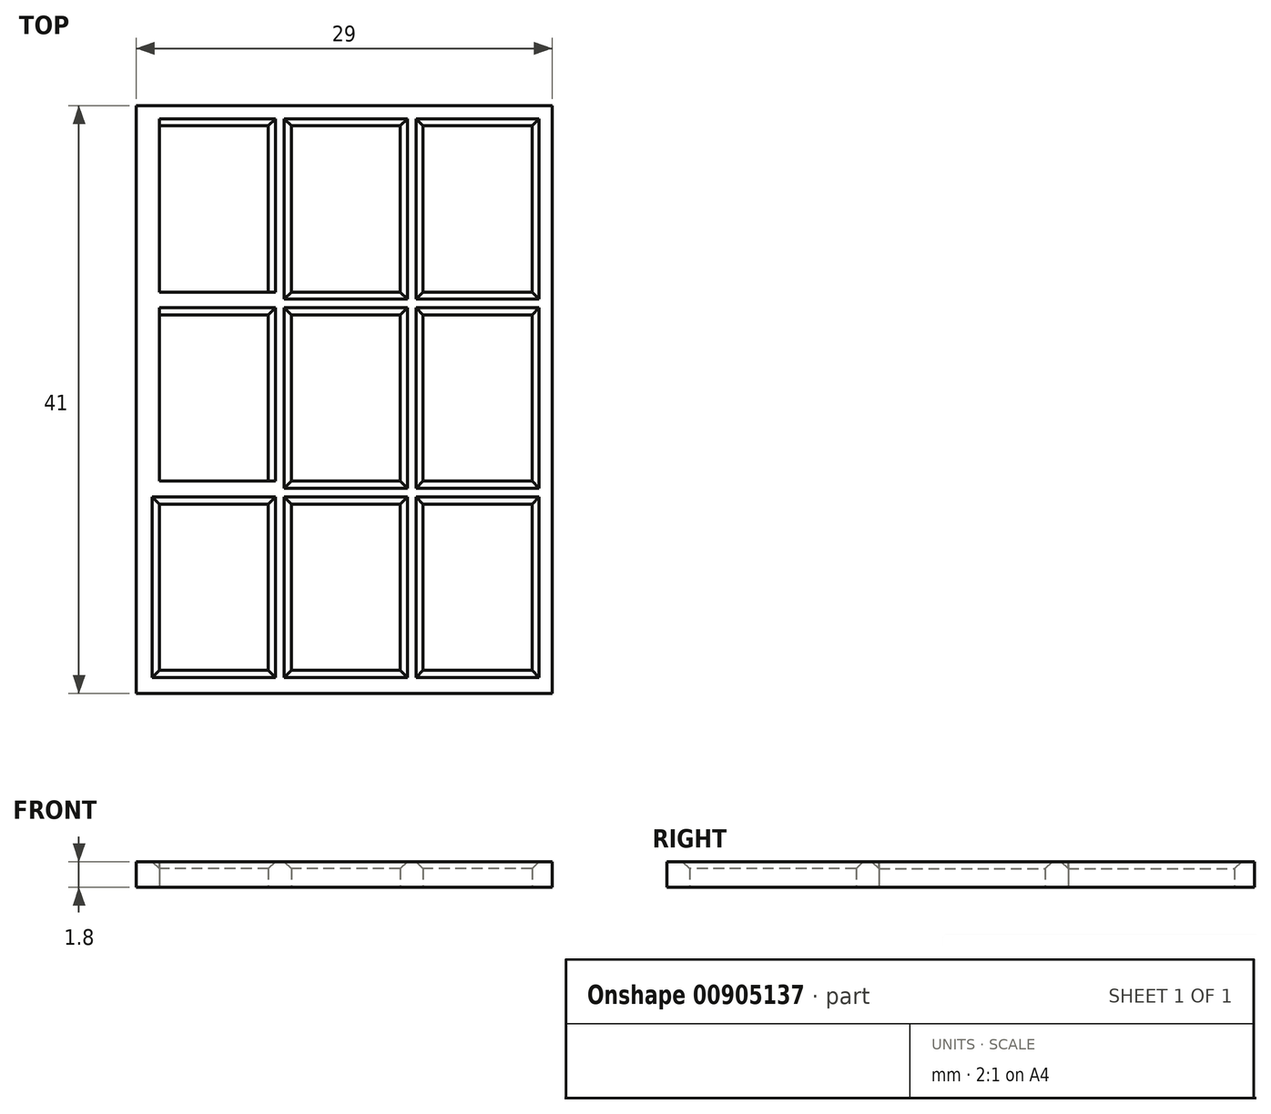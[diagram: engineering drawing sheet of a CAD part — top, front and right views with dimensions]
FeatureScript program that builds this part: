
annotation { "Feature Type Name" : "Feature", "Feature Type Description" : "" }
export const myFeature = defineFeature(function(context is Context, id is Id, definition is map)
    precondition{}
    {
        {
            var Q0;
            Q0=qCreatedBy(makeId("Top.planeOp"),FACE);
            var sketch = newSketch(context, id + "F0", { "sketchPlane" : qUnion([Q0])});
            skLineSegment(sketch, "E0.bottom", {"start": v(-14.5, -20.5) * mm, "end": v(14.5, -20.5) * mm});
            skLineSegment(sketch, "E0.top", {"start": v(-14.5, 20.5) * mm, "end": v(14.5, 20.5) * mm});
            skLineSegment(sketch, "E0.left", {"start": v(-14.5, -20.5) * mm, "end": v(-14.5, 20.5) * mm});
            skLineSegment(sketch, "E0.right", {"start": v(14.5, -20.5) * mm, "end": v(14.5, 20.5) * mm});
            skPoint(sketch, "E0.middle", {"position": v(0, 0) * mm});
            skLineSegment(sketch, "E1.bottom", {"start": v(-12.9, -18.9) * mm, "end": v(-5.3, -18.9) * mm});
            skLineSegment(sketch, "E1.left", {"start": v(-12.9, -18.9) * mm, "end": v(-12.9, -7.3) * mm});
            skLineSegment(sketch, "E2.top", {"start": v(-12.9, -7.3) * mm, "end": v(-5.3, -7.3) * mm});
            skLineSegment(sketch, "E2.right", {"start": v(-5.3, -18.9) * mm, "end": v(-5.3, -7.3) * mm});
            skLineSegment(sketch, "E3.1.0.0", {"start": v(-3.7, -7.3) * mm, "end": v(3.9, -7.3) * mm});
            skLineSegment(sketch, "E3.1.0.1", {"start": v(3.9, -18.9) * mm, "end": v(3.9, -7.3) * mm});
            skLineSegment(sketch, "E3.1.0.2", {"start": v(-3.7, -18.9) * mm, "end": v(3.9, -18.9) * mm});
            skLineSegment(sketch, "E3.1.0.3", {"start": v(-3.7, -18.9) * mm, "end": v(-3.7, -7.3) * mm});
            skLineSegment(sketch, "E3.2.0.0", {"start": v(5.5, -7.3) * mm, "end": v(13.1, -7.3) * mm});
            skLineSegment(sketch, "E3.2.0.1", {"start": v(13.1, -18.9) * mm, "end": v(13.1, -7.3) * mm});
            skLineSegment(sketch, "E3.2.0.2", {"start": v(5.5, -18.9) * mm, "end": v(13.1, -18.9) * mm});
            skLineSegment(sketch, "E3.2.0.3", {"start": v(5.5, -18.9) * mm, "end": v(5.5, -7.3) * mm});
            skLineSegment(sketch, "E4.0.1.0", {"start": v(-12.9, -5.7) * mm, "end": v(-12.9, 5.9) * mm});
            skLineSegment(sketch, "E4.0.1.1", {"start": v(5.5, -5.7) * mm, "end": v(13.1, -5.7) * mm});
            skLineSegment(sketch, "E4.0.1.2", {"start": v(3.9, -5.7) * mm, "end": v(3.9, 5.9) * mm});
            skLineSegment(sketch, "E4.0.1.3", {"start": v(5.5, -5.7) * mm, "end": v(5.5, 5.9) * mm});
            skLineSegment(sketch, "E4.0.1.4", {"start": v(-3.7, -5.7) * mm, "end": v(3.9, -5.7) * mm});
            skLineSegment(sketch, "E4.0.1.5", {"start": v(5.5, 5.9) * mm, "end": v(13.1, 5.9) * mm});
            skLineSegment(sketch, "E4.0.1.6", {"start": v(13.1, -5.7) * mm, "end": v(13.1, 5.9) * mm});
            skLineSegment(sketch, "E4.0.1.7", {"start": v(-12.9, 5.9) * mm, "end": v(-5.3, 5.9) * mm});
            skLineSegment(sketch, "E4.0.1.8", {"start": v(-5.3, -5.7) * mm, "end": v(-5.3, 5.9) * mm});
            skLineSegment(sketch, "E4.0.1.9", {"start": v(-3.7, -5.7) * mm, "end": v(-3.7, 5.9) * mm});
            skLineSegment(sketch, "E4.0.1.10", {"start": v(-3.7, 5.9) * mm, "end": v(3.9, 5.9) * mm});
            skLineSegment(sketch, "E4.0.1.11", {"start": v(-12.9, -5.7) * mm, "end": v(-5.3, -5.7) * mm});
            skLineSegment(sketch, "E4.0.1.12", {"start": v(-12.9, -5.7) * mm, "end": v(-5.3, -5.7) * mm});
            skLineSegment(sketch, "E4.0.1.13", {"start": v(-12.9, -5.7) * mm, "end": v(-12.9, 5.9) * mm});
            skLineSegment(sketch, "E4.0.2.0", {"start": v(-12.9, 7.5) * mm, "end": v(-12.9, 19.1) * mm});
            skLineSegment(sketch, "E4.0.2.1", {"start": v(5.5, 7.5) * mm, "end": v(13.1, 7.5) * mm});
            skLineSegment(sketch, "E4.0.2.2", {"start": v(3.9, 7.5) * mm, "end": v(3.9, 19.1) * mm});
            skLineSegment(sketch, "E4.0.2.3", {"start": v(5.5, 7.5) * mm, "end": v(5.5, 19.1) * mm});
            skLineSegment(sketch, "E4.0.2.4", {"start": v(-3.7, 7.5) * mm, "end": v(3.9, 7.5) * mm});
            skLineSegment(sketch, "E4.0.2.5", {"start": v(5.5, 19.1) * mm, "end": v(13.1, 19.1) * mm});
            skLineSegment(sketch, "E4.0.2.6", {"start": v(13.1, 7.5) * mm, "end": v(13.1, 19.1) * mm});
            skLineSegment(sketch, "E4.0.2.7", {"start": v(-12.9, 19.1) * mm, "end": v(-5.3, 19.1) * mm});
            skLineSegment(sketch, "E4.0.2.8", {"start": v(-5.3, 7.5) * mm, "end": v(-5.3, 19.1) * mm});
            skLineSegment(sketch, "E4.0.2.9", {"start": v(-3.7, 7.5) * mm, "end": v(-3.7, 19.1) * mm});
            skLineSegment(sketch, "E4.0.2.10", {"start": v(-3.7, 19.1) * mm, "end": v(3.9, 19.1) * mm});
            skLineSegment(sketch, "E4.0.2.11", {"start": v(-12.9, 7.5) * mm, "end": v(-5.3, 7.5) * mm});
            skLineSegment(sketch, "E4.0.2.12", {"start": v(-12.9, 7.5) * mm, "end": v(-5.3, 7.5) * mm});
            skLineSegment(sketch, "E4.0.2.13", {"start": v(-12.9, 7.5) * mm, "end": v(-12.9, 19.1) * mm});
            skLineSegment(sketch, "E4.direction1", {"start": v(-12.9, -18.9) * mm, "end": v(12.1, -18.9) * mm, "construction": true});
            skLineSegment(sketch, "E4.direction2", {"start": v(-12.9, -18.9) * mm, "end": v(-12.9, -5.7) * mm, "construction": true});
            skSolve(sketch);
        }
        {
            var Q0;
            Q0=makeQuery(id+"F0.imprint","IMPRINT",FACE,{"disambiguationData":[TD([[makeQuery(id+"F0.imprint","IMPRINT",EDGE,{"derivedFrom":sQuery(id+"F0.wireOp",EDGE,"E0.bottom")}),1.0]])]});
            extrude(context, id + "F1", {"entities" : qUnion([Q0]), "depth" : 1.8 * mm, "offsetDistance" : 25 * mm});
        }
        {
            var Q0;
            Q0=makeQuery(id+"F1.opExtrude","CAP_EDGE",EDGE,{"disambiguationData":[OSD([sQuery(id+"F0.wireOp",EDGE,"E4.0.2.7")])],"isStart":false});
            var Q1;
            Q1=makeQuery(id+"F1.opExtrude","CAP_EDGE",EDGE,{"disambiguationData":[OSD([sQuery(id+"F0.wireOp",EDGE,"E4.0.2.8")])],"isStart":false});
            var Q2;
            Q2=makeQuery(id+"F1.opExtrude","CAP_EDGE",EDGE,{"disambiguationData":[OSD([sQuery(id+"F0.wireOp",EDGE,"E4.0.2.13")])],"isStart":false});
            var Q3;
            Q3=makeQuery(id+"F1.opExtrude","CAP_EDGE",EDGE,{"disambiguationData":[OSD([sQuery(id+"F0.wireOp",EDGE,"E4.0.2.12")])],"isStart":false});
            var Q4;
            Q4=makeQuery(id+"F1.opExtrude","CAP_EDGE",EDGE,{"disambiguationData":[OSD([sQuery(id+"F0.wireOp",EDGE,"E4.0.2.4")])],"isStart":false});
            var Q5;
            Q5=makeQuery(id+"F1.opExtrude","CAP_EDGE",EDGE,{"disambiguationData":[OSD([sQuery(id+"F0.wireOp",EDGE,"E4.0.2.2")])],"isStart":false});
            var Q6;
            Q6=makeQuery(id+"F1.opExtrude","CAP_EDGE",EDGE,{"disambiguationData":[OSD([sQuery(id+"F0.wireOp",EDGE,"E4.0.2.10")])],"isStart":false});
            var Q7;
            Q7=makeQuery(id+"F1.opExtrude","CAP_EDGE",EDGE,{"disambiguationData":[OSD([sQuery(id+"F0.wireOp",EDGE,"E4.0.2.9")])],"isStart":false});
            var Q8;
            Q8=makeQuery(id+"F1.opExtrude","CAP_EDGE",EDGE,{"disambiguationData":[OSD([sQuery(id+"F0.wireOp",EDGE,"E4.0.2.5")])],"isStart":false});
            var Q9;
            Q9=makeQuery(id+"F1.opExtrude","CAP_EDGE",EDGE,{"disambiguationData":[OSD([sQuery(id+"F0.wireOp",EDGE,"E4.0.2.6")])],"isStart":false});
            var Q10;
            Q10=makeQuery(id+"F1.opExtrude","CAP_EDGE",EDGE,{"disambiguationData":[OSD([sQuery(id+"F0.wireOp",EDGE,"E4.0.2.1")])],"isStart":false});
            var Q11;
            Q11=makeQuery(id+"F1.opExtrude","CAP_EDGE",EDGE,{"disambiguationData":[OSD([sQuery(id+"F0.wireOp",EDGE,"E4.0.2.3")])],"isStart":false});
            var Q12;
            Q12=makeQuery(id+"F1.opExtrude","CAP_EDGE",EDGE,{"disambiguationData":[OSD([sQuery(id+"F0.wireOp",EDGE,"E4.0.1.7")])],"isStart":false});
            var Q13;
            Q13=makeQuery(id+"F1.opExtrude","CAP_EDGE",EDGE,{"disambiguationData":[OSD([sQuery(id+"F0.wireOp",EDGE,"E4.0.1.8")])],"isStart":false});
            var Q14;
            Q14=makeQuery(id+"F1.opExtrude","CAP_EDGE",EDGE,{"disambiguationData":[OSD([sQuery(id+"F0.wireOp",EDGE,"E4.0.1.12")])],"isStart":false});
            var Q15;
            Q15=makeQuery(id+"F1.opExtrude","CAP_EDGE",EDGE,{"disambiguationData":[OSD([sQuery(id+"F0.wireOp",EDGE,"E4.0.1.13")])],"isStart":false});
            var Q16;
            Q16=makeQuery(id+"F1.opExtrude","CAP_EDGE",EDGE,{"disambiguationData":[OSD([sQuery(id+"F0.wireOp",EDGE,"E4.0.1.9")])],"isStart":false});
            var Q17;
            Q17=makeQuery(id+"F1.opExtrude","CAP_EDGE",EDGE,{"disambiguationData":[OSD([sQuery(id+"F0.wireOp",EDGE,"E4.0.1.10")])],"isStart":false});
            var Q18;
            Q18=makeQuery(id+"F1.opExtrude","CAP_EDGE",EDGE,{"disambiguationData":[OSD([sQuery(id+"F0.wireOp",EDGE,"E4.0.1.2")])],"isStart":false});
            var Q19;
            Q19=makeQuery(id+"F1.opExtrude","CAP_EDGE",EDGE,{"disambiguationData":[OSD([sQuery(id+"F0.wireOp",EDGE,"E4.0.1.4")])],"isStart":false});
            var Q20;
            Q20=makeQuery(id+"F1.opExtrude","CAP_EDGE",EDGE,{"disambiguationData":[OSD([sQuery(id+"F0.wireOp",EDGE,"E4.0.1.1")])],"isStart":false});
            var Q21;
            Q21=makeQuery(id+"F1.opExtrude","CAP_EDGE",EDGE,{"disambiguationData":[OSD([sQuery(id+"F0.wireOp",EDGE,"E4.0.1.3")])],"isStart":false});
            var Q22;
            Q22=makeQuery(id+"F1.opExtrude","CAP_EDGE",EDGE,{"disambiguationData":[OSD([sQuery(id+"F0.wireOp",EDGE,"E4.0.1.5")])],"isStart":false});
            var Q23;
            Q23=makeQuery(id+"F1.opExtrude","CAP_EDGE",EDGE,{"disambiguationData":[OSD([sQuery(id+"F0.wireOp",EDGE,"E4.0.1.6")])],"isStart":false});
            var Q24;
            Q24=makeQuery(id+"F1.opExtrude","CAP_EDGE",EDGE,{"disambiguationData":[OSD([sQuery(id+"F0.wireOp",EDGE,"E3.2.0.0")])],"isStart":false});
            var Q25;
            Q25=makeQuery(id+"F1.opExtrude","CAP_EDGE",EDGE,{"disambiguationData":[OSD([sQuery(id+"F0.wireOp",EDGE,"E3.2.0.1")])],"isStart":false});
            var Q26;
            Q26=makeQuery(id+"F1.opExtrude","CAP_EDGE",EDGE,{"disambiguationData":[OSD([sQuery(id+"F0.wireOp",EDGE,"E3.2.0.2")])],"isStart":false});
            var Q27;
            Q27=makeQuery(id+"F1.opExtrude","CAP_EDGE",EDGE,{"disambiguationData":[OSD([sQuery(id+"F0.wireOp",EDGE,"E3.2.0.3")])],"isStart":false});
            var Q28;
            Q28=makeQuery(id+"F1.opExtrude","CAP_EDGE",EDGE,{"disambiguationData":[OSD([sQuery(id+"F0.wireOp",EDGE,"E3.1.0.0")])],"isStart":false});
            var Q29;
            Q29=makeQuery(id+"F1.opExtrude","CAP_EDGE",EDGE,{"disambiguationData":[OSD([sQuery(id+"F0.wireOp",EDGE,"E3.1.0.3")])],"isStart":false});
            var Q30;
            Q30=makeQuery(id+"F1.opExtrude","CAP_EDGE",EDGE,{"disambiguationData":[OSD([sQuery(id+"F0.wireOp",EDGE,"E3.1.0.2")])],"isStart":false});
            var Q31;
            Q31=makeQuery(id+"F1.opExtrude","CAP_EDGE",EDGE,{"disambiguationData":[OSD([sQuery(id+"F0.wireOp",EDGE,"E3.1.0.1")])],"isStart":false});
            var Q32;
            Q32=makeQuery(id+"F1.opExtrude","CAP_EDGE",EDGE,{"disambiguationData":[OSD([sQuery(id+"F0.wireOp",EDGE,"E2.top")])],"isStart":false});
            var Q33;
            Q33=makeQuery(id+"F1.opExtrude","CAP_EDGE",EDGE,{"disambiguationData":[OSD([sQuery(id+"F0.wireOp",EDGE,"E2.right")])],"isStart":false});
            var Q34;
            Q34=makeQuery(id+"F1.opExtrude","CAP_EDGE",EDGE,{"disambiguationData":[OSD([sQuery(id+"F0.wireOp",EDGE,"E1.bottom")])],"isStart":false});
            var Q35;
            Q35=makeQuery(id+"F1.opExtrude","CAP_EDGE",EDGE,{"disambiguationData":[OSD([sQuery(id+"F0.wireOp",EDGE,"E1.left")])],"isStart":false});
            chamfer(context, id + "F2", {"entities" : qUnion([Q0, Q1, Q2, Q3, Q4, Q5, Q6, Q7, Q8, Q9, Q10, Q11, Q12, Q13, Q14, Q15, Q16, Q17, Q18, Q19, Q20, Q21, Q22, Q23, Q24, Q25, Q26, Q27, Q28, Q29, Q30, Q31, Q32, Q33, Q34, Q35]), "width" : .5 * mm, "tangentPropagation" : true});
        }
    });
